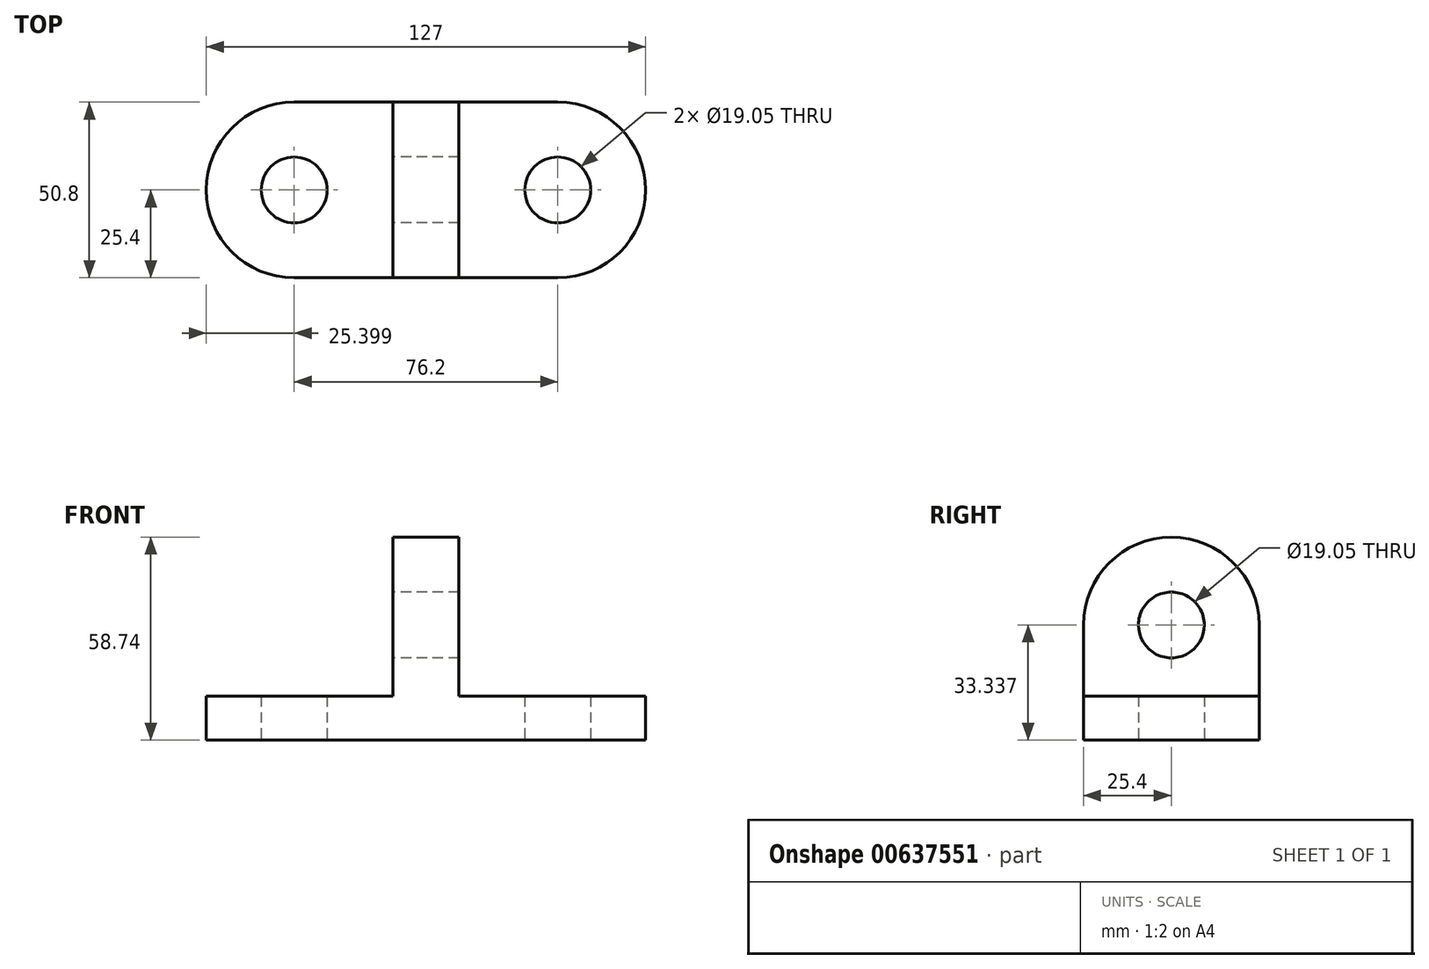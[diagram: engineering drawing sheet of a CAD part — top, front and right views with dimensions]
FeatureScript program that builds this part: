
annotation { "Feature Type Name" : "Feature", "Feature Type Description" : "" }
export const myFeature = defineFeature(function(context is Context, id is Id, definition is map)
    precondition{}
    {
        {
            var Q0;
            Q0=qCreatedBy(makeId("Top.planeOp"),FACE);
            var sketch = newSketch(context, id + "F0", { "sketchPlane" : qUnion([Q0])});
            skLineSegment(sketch, "E0", {"start": v(-48.58, 0) * mm, "end": v(27.62, 0) * mm});
            skLineSegment(sketch, "E1", {"start": v(27.62, 0) * mm, "end": v(27.62, 50.8) * mm});
            skLineSegment(sketch, "E2", {"start": v(-48.58, 0) * mm, "end": v(-48.58, 50.8) * mm});
            skLineSegment(sketch, "E3", {"start": v(-48.58, 50.8) * mm, "end": v(27.62, 50.8) * mm});
            skLineSegment(sketch, "E4", {"start": v(-48.58, 50.8) * mm, "end": v(-48.58, 25.4) * mm});
            skLineSegment(sketch, "E5", {"start": v(27.62, 50.8) * mm, "end": v(27.62, 25.4) * mm});
            skCircle(sketch, "E6", {"center": v(-48.58, 25.4) * mm, "radius": 9.53 * mm});
            skCircle(sketch, "E7", {"center": v(27.62, 25.4) * mm, "radius": 9.53 * mm});
            skArc(sketch, "E8", {"start": v(-48.58, 50.8) * mm, "mid": v(-73.98, 25.4) * mm, "end": v(-48.58, 0) * mm});
            skArc(sketch, "E9", {"start": v(27.62, 0) * mm, "mid": v(53.02, 25.4) * mm, "end": v(27.62, 50.8) * mm});
            skLineSegment(sketch, "E10", {"start": v(27.62, 0) * mm, "end": v(-10.48, 0) * mm});
            skSolve(sketch);
        }
        {
            var Q0;
            {var subQ2=sQuery(id+"F0.wireOp",EDGE,"E0");Q0=makeQuery(id+"F0.imprint","IMPRINT",FACE,{"disambiguationData":[TD([[makeQuery(id+"F0.imprint","IMPRINT",EDGE,{"derivedFrom":subQ2}),1.0]])]});}
            var Q1;
            {var subQ0=sQuery(id+"F0.wireOp",EDGE,"E8");Q1=makeQuery(id+"F0.imprint","IMPRINT",FACE,{"disambiguationData":[TD([[makeQuery(id+"F0.imprint","IMPRINT",EDGE,{"derivedFrom":subQ0}),1.0]])]});}
            var Q2;
            {var subQ0=sQuery(id+"F0.wireOp",EDGE,"E9");Q2=makeQuery(id+"F0.imprint","IMPRINT",FACE,{"disambiguationData":[TD([[makeQuery(id+"F0.imprint","IMPRINT",EDGE,{"derivedFrom":subQ0}),1.0]])]});}
            extrude(context, id + "F1", {"entities" : qUnion([Q0, Q1, Q2]), "depth" : 12.7 * mm, "offsetDistance" : 25.4 * mm});
        }
        {
            var Q0;
            Q0=makeQuery(id+"F1.opExtrude","CAP_FACE",FACE,{"disambiguationData":[OSD([sQuery(id+"F0.wireOp",EDGE,"E0"),sQuery(id+"F0.wireOp",EDGE,"E3"),sQuery(id+"F0.wireOp",EDGE,"E6"),sQuery(id+"F0.wireOp",EDGE,"E7"),sQuery(id+"F0.wireOp",EDGE,"E8"),sQuery(id+"F0.wireOp",EDGE,"E9")])],"isStart":false});
            var sketch = newSketch(context, id + "F2", { "sketchPlane" : qUnion([Q0])});
            skLineSegment(sketch, "E11", {"start": v(-20, 0) * mm, "end": v(-20, 50.8) * mm});
            skLineSegment(sketch, "E12", {"start": v(-10.48, 50.8) * mm, "end": v(-20, 50.8) * mm});
            skLineSegment(sketch, "E13", {"start": v(-10.48, 50.8) * mm, "end": v(-0.96, 50.8) * mm});
            skLineSegment(sketch, "E14", {"start": v(-0.96, 50.8) * mm, "end": v(-0.96, 0) * mm});
            skLineSegment(sketch, "E15", {"start": v(-0.96, 0) * mm, "end": v(-20, 0) * mm});
            skSolve(sketch);
        }
        {
            var Q0;
            {var subQ0=sQuery(id+"F2.wireOp",EDGE,"5ZgEYW8W-U2vx-O0oR-WLCF-laBODHadYTwy");Q0=makeQuery(id+"F2.imprint","IMPRINT",FACE,{"disambiguationData":[TD([[makeQuery(id+"F2.imprint","IMPRINT",EDGE,{"derivedFrom":subQ0}),1.0]])]});}
            var Q1;
            Q1=makeQuery(id+"F2.imprint","IMPRINT",FACE,{"disambiguationData":[TD([[makeQuery(id+"F2.imprint","IMPRINT",EDGE,{"derivedFrom":sQuery(id+"F2.wireOp",EDGE,"E11")}),-1.0]])]});
            extrude(context, id + "F3", {"entities" : qUnion([Q0, Q1]), "operationType" : NewBodyOperationType.ADD, "depth" : 20.64 * mm, "offsetDistance" : 25.4 * mm});
        }
        {
            var Q0;
            Q0=makeQuery(id+"F3.opExtrude","SWEPT_FACE",FACE,{"disambiguationData":[OSD([sQuery(id+"F2.wireOp",EDGE,"E11")])]});
            var sketch = newSketch(context, id + "F4", { "sketchPlane" : qUnion([Q0])});
            skArc(sketch, "E16", {"start": v(0, 33.34) * mm, "mid": v(-25.4, 58.74) * mm, "end": v(-50.8, 33.34) * mm});
            skSolve(sketch);
        }
        {
            var Q0;
            Q0=makeQuery(id+"F4.imprint","IMPRINT",FACE,{"disambiguationData":[TD([[makeQuery(id+"F4.imprint","IMPRINT",EDGE,{"derivedFrom":sQuery(id+"F4.wireOp",EDGE,"E16")}),1.0]])]});
            extrude(context, id + "F5", {"entities" : qUnion([Q0]), "operationType" : NewBodyOperationType.ADD, "oppositeDirection" : true, "depth" : 19.05 * mm, "offsetDistance" : 25.4 * mm});
        }
        {
            var Q0;
            {var subQ0=sQuery(id+"F2.wireOp",EDGE,"E11");Q0=makeQuery(id+"F5.boolean.opBoolean","MERGE",FACE,{"derivedFrom":[makeQuery(id+"F3.opExtrude","SWEPT_FACE",FACE,{"disambiguationData":[OSD([subQ0])]}),makeQuery(id+"F5.opExtrude","CAP_FACE",FACE,{"disambiguationData":[OSD([subQ0,sQuery(id+"F4.wireOp",EDGE,"E16")])],"isStart":true})]});}
            var sketch = newSketch(context, id + "F6", { "sketchPlane" : qUnion([Q0])});
            skCircle(sketch, "E17", {"center": v(-25.4, 33.34) * mm, "radius": 9.53 * mm});
            skSolve(sketch);
        }
        {
            var Q0;
            Q0=makeQuery(id+"F6.imprint","IMPRINT",FACE,{"disambiguationData":[TD([[makeQuery(id+"F6.imprint","IMPRINT",EDGE,{"derivedFrom":sQuery(id+"F6.wireOp",EDGE,"E17")}),1.0]])]});
            extrude(context, id + "F7", {"entities" : qUnion([Q0]), "operationType" : NewBodyOperationType.REMOVE, "oppositeDirection" : true, "depth" : 19.05 * mm, "offsetDistance" : 25.4 * mm});
        }
    });
